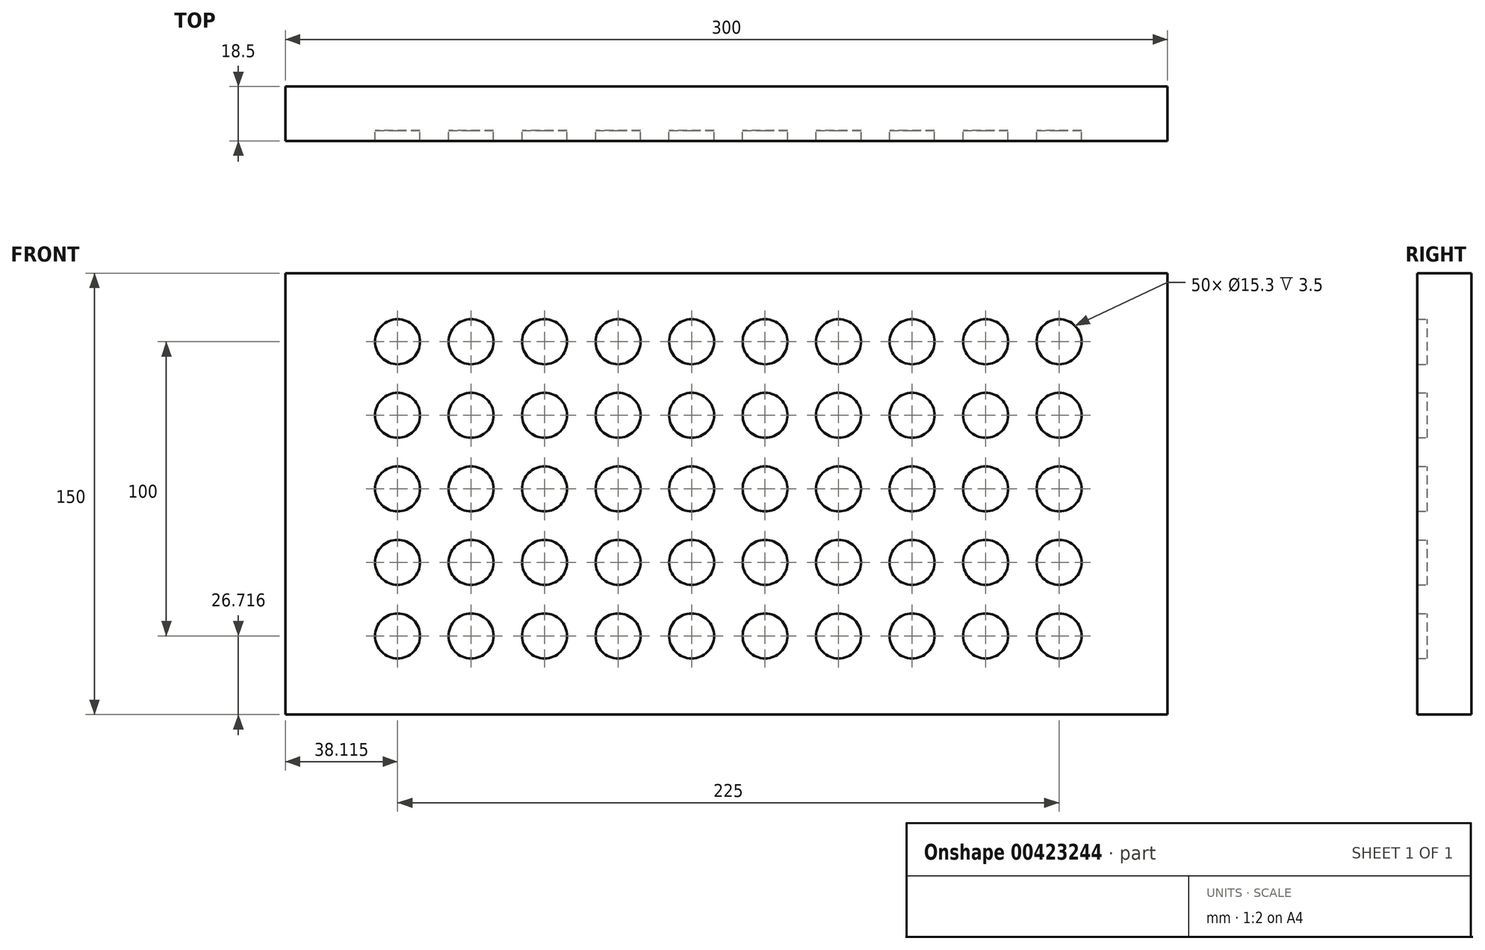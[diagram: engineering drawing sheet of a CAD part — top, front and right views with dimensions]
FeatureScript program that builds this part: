
annotation { "Feature Type Name" : "Feature", "Feature Type Description" : "" }
export const myFeature = defineFeature(function(context is Context, id is Id, definition is map)
    precondition{}
    {
        {
            var Q0;
            Q0=qCreatedBy(makeId("Front.planeOp"),FACE);
            var sketch = newSketch(context, id + "F0", { "sketchPlane" : qUnion([Q0])});
            skCircle(sketch, "E0", {"center": v(-292.16, 29.74) * mm, "radius": 7.65 * mm});
            skCircle(sketch, "E1.0.1.0", {"center": v(-292.16, 54.74) * mm, "radius": 7.65 * mm});
            skCircle(sketch, "E1.0.2.0", {"center": v(-292.16, 79.74) * mm, "radius": 7.65 * mm});
            skCircle(sketch, "E1.0.3.0", {"center": v(-292.16, 104.74) * mm, "radius": 7.65 * mm});
            skCircle(sketch, "E1.0.4.0", {"center": v(-292.16, 129.74) * mm, "radius": 7.65 * mm});
            skCircle(sketch, "E1.1.0.0", {"center": v(-267.16, 29.74) * mm, "radius": 7.65 * mm});
            skCircle(sketch, "E1.1.1.0", {"center": v(-267.16, 54.74) * mm, "radius": 7.65 * mm});
            skCircle(sketch, "E1.1.2.0", {"center": v(-267.16, 79.74) * mm, "radius": 7.65 * mm});
            skCircle(sketch, "E1.1.3.0", {"center": v(-267.16, 104.74) * mm, "radius": 7.65 * mm});
            skCircle(sketch, "E1.1.4.0", {"center": v(-267.16, 129.74) * mm, "radius": 7.65 * mm});
            skCircle(sketch, "E1.2.0.0", {"center": v(-242.16, 29.74) * mm, "radius": 7.65 * mm});
            skCircle(sketch, "E1.2.1.0", {"center": v(-242.16, 54.74) * mm, "radius": 7.65 * mm});
            skCircle(sketch, "E1.2.2.0", {"center": v(-242.16, 79.74) * mm, "radius": 7.65 * mm});
            skCircle(sketch, "E1.2.3.0", {"center": v(-242.16, 104.74) * mm, "radius": 7.65 * mm});
            skCircle(sketch, "E1.2.4.0", {"center": v(-242.16, 129.74) * mm, "radius": 7.65 * mm});
            skCircle(sketch, "E1.3.0.0", {"center": v(-217.16, 29.74) * mm, "radius": 7.65 * mm});
            skCircle(sketch, "E1.3.1.0", {"center": v(-217.16, 54.74) * mm, "radius": 7.65 * mm});
            skCircle(sketch, "E1.3.2.0", {"center": v(-217.16, 79.74) * mm, "radius": 7.65 * mm});
            skCircle(sketch, "E1.3.3.0", {"center": v(-217.16, 104.74) * mm, "radius": 7.65 * mm});
            skCircle(sketch, "E1.3.4.0", {"center": v(-217.16, 129.74) * mm, "radius": 7.65 * mm});
            skCircle(sketch, "E1.4.0.0", {"center": v(-192.16, 29.74) * mm, "radius": 7.65 * mm});
            skCircle(sketch, "E1.4.1.0", {"center": v(-192.16, 54.74) * mm, "radius": 7.65 * mm});
            skCircle(sketch, "E1.4.2.0", {"center": v(-192.16, 79.74) * mm, "radius": 7.65 * mm});
            skCircle(sketch, "E1.4.3.0", {"center": v(-192.16, 104.74) * mm, "radius": 7.65 * mm});
            skCircle(sketch, "E1.4.4.0", {"center": v(-192.16, 129.74) * mm, "radius": 7.65 * mm});
            skCircle(sketch, "E1.5.0.0", {"center": v(-167.16, 29.74) * mm, "radius": 7.65 * mm});
            skCircle(sketch, "E1.5.1.0", {"center": v(-167.16, 54.74) * mm, "radius": 7.65 * mm});
            skCircle(sketch, "E1.5.2.0", {"center": v(-167.16, 79.74) * mm, "radius": 7.65 * mm});
            skCircle(sketch, "E1.5.3.0", {"center": v(-167.16, 104.74) * mm, "radius": 7.65 * mm});
            skCircle(sketch, "E1.5.4.0", {"center": v(-167.16, 129.74) * mm, "radius": 7.65 * mm});
            skCircle(sketch, "E1.6.0.0", {"center": v(-142.16, 29.74) * mm, "radius": 7.65 * mm});
            skCircle(sketch, "E1.6.1.0", {"center": v(-142.16, 54.74) * mm, "radius": 7.65 * mm});
            skCircle(sketch, "E1.6.2.0", {"center": v(-142.16, 79.74) * mm, "radius": 7.65 * mm});
            skCircle(sketch, "E1.6.3.0", {"center": v(-142.16, 104.74) * mm, "radius": 7.65 * mm});
            skCircle(sketch, "E1.6.4.0", {"center": v(-142.16, 129.74) * mm, "radius": 7.65 * mm});
            skCircle(sketch, "E1.7.0.0", {"center": v(-117.16, 29.74) * mm, "radius": 7.65 * mm});
            skCircle(sketch, "E1.7.1.0", {"center": v(-117.16, 54.74) * mm, "radius": 7.65 * mm});
            skCircle(sketch, "E1.7.2.0", {"center": v(-117.16, 79.74) * mm, "radius": 7.65 * mm});
            skCircle(sketch, "E1.7.3.0", {"center": v(-117.16, 104.74) * mm, "radius": 7.65 * mm});
            skCircle(sketch, "E1.7.4.0", {"center": v(-117.16, 129.74) * mm, "radius": 7.65 * mm});
            skCircle(sketch, "E1.8.0.0", {"center": v(-92.16, 29.74) * mm, "radius": 7.65 * mm});
            skCircle(sketch, "E1.8.1.0", {"center": v(-92.16, 54.74) * mm, "radius": 7.65 * mm});
            skCircle(sketch, "E1.8.2.0", {"center": v(-92.16, 79.74) * mm, "radius": 7.65 * mm});
            skCircle(sketch, "E1.8.3.0", {"center": v(-92.16, 104.74) * mm, "radius": 7.65 * mm});
            skCircle(sketch, "E1.8.4.0", {"center": v(-92.16, 129.74) * mm, "radius": 7.65 * mm});
            skCircle(sketch, "E1.9.0.0", {"center": v(-67.16, 29.74) * mm, "radius": 7.65 * mm});
            skCircle(sketch, "E1.9.1.0", {"center": v(-67.16, 54.74) * mm, "radius": 7.65 * mm});
            skCircle(sketch, "E1.9.2.0", {"center": v(-67.16, 79.74) * mm, "radius": 7.65 * mm});
            skCircle(sketch, "E1.9.3.0", {"center": v(-67.16, 104.74) * mm, "radius": 7.65 * mm});
            skCircle(sketch, "E1.9.4.0", {"center": v(-67.16, 129.74) * mm, "radius": 7.65 * mm});
            skLineSegment(sketch, "E1.direction1", {"start": v(-292.16, 29.74) * mm, "end": v(-267.16, 29.74) * mm, "construction": true});
            skLineSegment(sketch, "E1.direction2", {"start": v(-292.16, 29.74) * mm, "end": v(-292.16, 54.74) * mm, "construction": true});
            skLineSegment(sketch, "E2.bottom", {"start": v(-330.28, 153.02) * mm, "end": v(-30.28, 153.02) * mm});
            skLineSegment(sketch, "E2.top", {"start": v(-330.28, 3.02) * mm, "end": v(-30.28, 3.02) * mm});
            skLineSegment(sketch, "E2.left", {"start": v(-330.28, 153.02) * mm, "end": v(-330.28, 3.02) * mm});
            skLineSegment(sketch, "E2.right", {"start": v(-30.28, 153.02) * mm, "end": v(-30.28, 3.02) * mm});
            skSolve(sketch);
        }
        {
            var Q0;
            Q0=makeQuery(id+"F0.imprint","IMPRINT",FACE,{"disambiguationData":[TD([[makeQuery(id+"F0.imprint","IMPRINT",EDGE,{"derivedFrom":sQuery(id+"F0.wireOp",EDGE,"E0")}),-1.0]])]});
            extrude(context, id + "F1", {"entities" : qUnion([Q0]), "depth" : 3.5 * mm});
        }
        {
            var Q0;
            Q0=qCreatedBy(makeId("Front.planeOp"),FACE);
            var sketch = newSketch(context, id + "F2", { "sketchPlane" : qUnion([Q0])});
            skPoint(sketch, "E3.0", {"position": v(-30.28, 153.02) * mm});
            skPoint(sketch, "E4.0", {"position": v(-330.28, 153.02) * mm});
            skPoint(sketch, "E5.0", {"position": v(-330.28, 3.02) * mm});
            skPoint(sketch, "E6.0", {"position": v(-30.28, 3.02) * mm});
            skLineSegment(sketch, "E7", {"start": v(-30.28, 153.02) * mm, "end": v(-330.28, 153.02) * mm});
            skLineSegment(sketch, "E8", {"start": v(-330.28, 153.02) * mm, "end": v(-330.28, 3.02) * mm});
            skLineSegment(sketch, "E9", {"start": v(-330.28, 3.02) * mm, "end": v(-30.28, 3.02) * mm});
            skLineSegment(sketch, "E10", {"start": v(-30.28, 3.02) * mm, "end": v(-30.28, 153.02) * mm});
            skSolve(sketch);
        }
        {
            var Q0;
            Q0=makeQuery(id+"F2.imprint","IMPRINT",FACE,{"disambiguationData":[TD([[makeQuery(id+"F2.imprint","IMPRINT",EDGE,{"derivedFrom":sQuery(id+"F2.wireOp",EDGE,"E7")}),1.0]])]});
            extrude(context, id + "F3", {"entities" : qUnion([Q0]), "operationType" : NewBodyOperationType.ADD, "oppositeDirection" : true, "depth" : 15 * mm});
        }
    });
